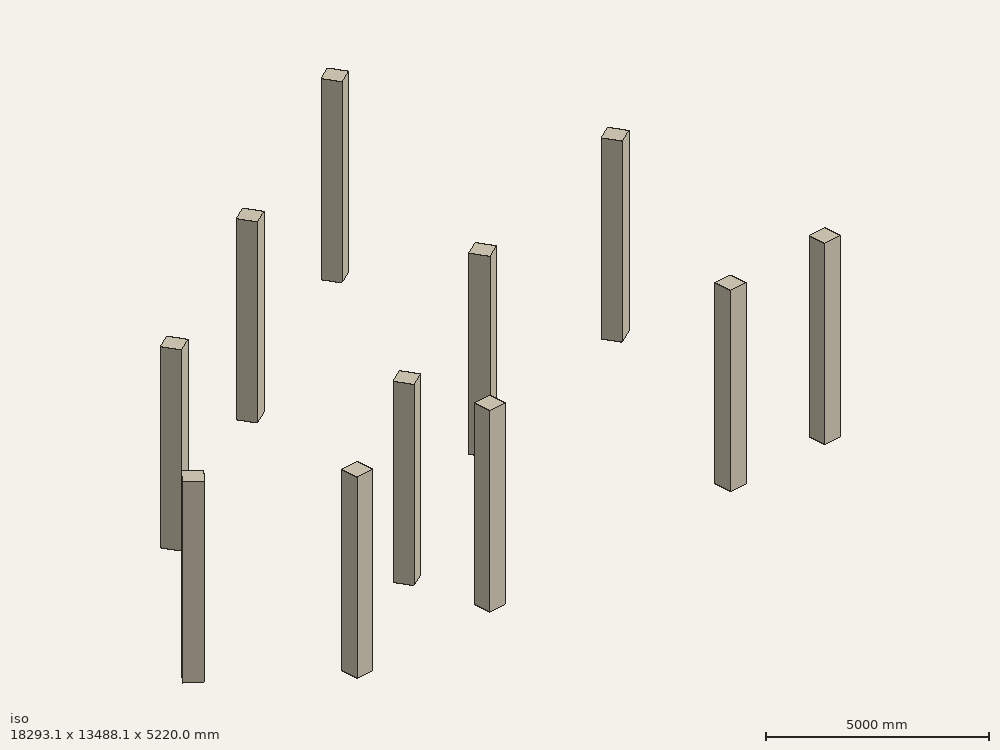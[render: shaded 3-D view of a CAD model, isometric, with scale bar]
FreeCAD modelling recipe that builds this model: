
FCSTD DOCUMENT  (FreeCAD 0.21R32165 (Git))
Label: test
License: All rights reserved
LicenseURL: http://en.wikipedia.org/wiki/All_rights_reserved
objects: Part::FeaturePython×27, Part::Part2DObjectPython×13, App::DocumentObjectGroup×2, App::FeaturePython×1
note: 40 computed .brp shape members not serialized (recipe doc carries the construction recipe); baked Part::Feature solids carry a one-line shape summary decoded from their .brp

FEATURE [Part::Part2DObjectPython] Line  label="C1_STORY1_CenterLine"  # Draft 2D object (typed FeaturePython)
  Area = 0
  ChamferSize = 0
  Closed = false
  End = (2820,0,5220)
  FilletRadius = 0
  Length = 5220
  MakeFace = true
  Points = (2) [(2820,0,0),(2820,0,5220)]
  Start = (2820,0,0)
  Subdivisions = 0
FEATURE [Part::Part2DObjectPython] C5016F20  # Draft 2D object (typed FeaturePython)
  Height = 500
  Width = 500
FEATURE [Part::FeaturePython] Structure  label="C1_STORY1"  # Arch/BIM 24 (typed FeaturePython)
  AttacherType = Attacher::AttachEngine3D
  AttachmentOffset = pos=(0,0,0) rot=(0,0,1;1.5708rad)
  Base = -> C5016F20
  BaseMirror = false
  BaseOffsetX = 0
  BaseOffsetY = 0
  BasePerpendicularToTool = false
  BaseRotation = 0
  ComputedLength = 5220
  FaceMaker = 0
  Height = 5220
  HorizontalArea = 250000
  IfcData = attributes={"GlobalId": {"name": "GlobalId", "type": "IfcGloballyUniqueId", "is_enum": false, "enum_values": []}, "Description": {"... (+438 chars omitted),+1 more (map truncated)
  IfcType = 24
  Length = 0
  MapMode = 7
  MoveBase = false
  MoveWithHost = false
  Nodes = (2) [(2820,0,0),(2820,0,5220)]
  NodesOffset = 0
  Normal = (0,0,0)
  PerimeterLength = 2000
  Placement = pos=(2820,0,0) rot=(0,0,1;1.5708rad)
  PredefinedType = 0
  Support = -> [Line]
  ToolOffsetFirst = 0
  ToolOffsetLast = 0
  VerticalArea = 1.044e+07
  Width = 100
  combos_load = COMB1 Max=367.7152, 16546.99, 15948.15,COMB10 Max=-248.3503, 396220.92, -73103.59,COMB11 Max=-87.283, 359070.73, 131552.42,+32 more (map truncated)
FEATURE [Part::Part2DObjectPython] Line001  label="C2_STORY1_CenterLine"  # Draft 2D object (typed FeaturePython)
  Area = 0
  ChamferSize = 0
  Closed = false
  End = (7040,0,5220)
  FilletRadius = 0
  Length = 5220
  MakeFace = true
  Points = (2) [(7040,0,0),(7040,0,5220)]
  Start = (7040,0,0)
  Subdivisions = 0
FEATURE [Part::FeaturePython] Structure001  label="C2_STORY1"  # Arch/BIM 24 (typed FeaturePython)
  AttacherType = Attacher::AttachEngine3D
  AttachmentOffset = pos=(0,0,0) rot=(0,0,1;1.5708rad)
  Base = -> C5016F20
  BaseMirror = false
  BaseOffsetX = 0
  BaseOffsetY = 0
  BasePerpendicularToTool = false
  BaseRotation = 0
  ComputedLength = 5220
  FaceMaker = 0
  Height = 5220
  HorizontalArea = 250000
  IfcData = attributes={"GlobalId": {"name": "GlobalId", "type": "IfcGloballyUniqueId", "is_enum": false, "enum_values": []}, "Description": {"... (+438 chars omitted),+1 more (map truncated)
  IfcType = 24
  Length = 0
  MapMode = 7
  MoveBase = false
  MoveWithHost = false
  Nodes = (2) [(7040,0,0),(7040,0,5220)]
  NodesOffset = 0
  Normal = (0,0,0)
  PerimeterLength = 2000
  Placement = pos=(7040,0,0) rot=(0,0,1;1.5708rad)
  PredefinedType = 0
  Support = -> [Line001]
  ToolOffsetFirst = 0
  ToolOffsetLast = 0
  VerticalArea = 1.044e+07
  Width = 100
  combos_load = COMB1 Max=587.8077, 16723.54, 23204.84,COMB10 Max=-181.5024, 376105.16, -60381.43,COMB11 Max=-325.9834, 365440.67, 122246.28,+32 more (map truncated)
FEATURE [Part::Part2DObjectPython] Line002  label="C3_STORY1_CenterLine"  # Draft 2D object (typed FeaturePython)
  Area = 0
  ChamferSize = 0
  Closed = false
  End = (14690,0,5220)
  FilletRadius = 0
  Length = 5220
  MakeFace = true
  Points = (2) [(14690,0,0),(14690,0,5220)]
  Start = (14690,0,0)
  Subdivisions = 0
FEATURE [Part::Part2DObjectPython] C5016F18  # Draft 2D object (typed FeaturePython)
  Height = 500
  Width = 500
FEATURE [Part::FeaturePython] Structure002  label="C3_STORY1"  # Arch/BIM 24 (typed FeaturePython)
  AttacherType = Attacher::AttachEngine3D
  AttachmentOffset = pos=(0,0,0) rot=(0,0,1;1.5708rad)
  Base = -> C5016F18
  BaseMirror = false
  BaseOffsetX = 0
  BaseOffsetY = 0
  BasePerpendicularToTool = false
  BaseRotation = 0
  ComputedLength = 5220
  FaceMaker = 0
  Height = 5220
  HorizontalArea = 250000
  IfcData = attributes={"GlobalId": {"name": "GlobalId", "type": "IfcGloballyUniqueId", "is_enum": false, "enum_values": []}, "Description": {"... (+438 chars omitted),+1 more (map truncated)
  IfcType = 24
  Length = 0
  MapMode = 7
  MoveBase = false
  MoveWithHost = false
  Nodes = (2) [(14690,0,0),(14690,0,5220)]
  NodesOffset = 0
  Normal = (0,0,0)
  PerimeterLength = 2000
  Placement = pos=(14690,0,0) rot=(0,0,1;1.5708rad)
  PredefinedType = 0
  Support = -> [Line002]
  ToolOffsetFirst = 0
  ToolOffsetLast = 0
  VerticalArea = 1.044e+07
  Width = 100
  combos_load = COMB1 Max=902.7233, -626.5, -12843.09,COMB10 Max=479.9441, 305538.87, -85269.26,COMB11 Max=651.8424, 341909.32, 114529.19,+32 more (map truncated)
FEATURE [Part::Part2DObjectPython] Line003  label="C4_STORY1_CenterLine"  # Draft 2D object (typed FeaturePython)
  Area = 0
  ChamferSize = 0
  Closed = false
  End = (17690,0,5220)
  FilletRadius = 0
  Length = 5220
  MakeFace = true
  Points = (2) [(17690,0,0),(17690,0,5220)]
  Start = (17690,0,0)
  Subdivisions = 0
FEATURE [Part::FeaturePython] Structure003  label="C4_STORY1"  # Arch/BIM 24 (typed FeaturePython)
  AttacherType = Attacher::AttachEngine3D
  AttachmentOffset = pos=(0,0,0) rot=(0,0,1;1.5708rad)
  Base = -> C5016F20
  BaseMirror = false
  BaseOffsetX = 0
  BaseOffsetY = 0
  BasePerpendicularToTool = false
  BaseRotation = 0
  ComputedLength = 5220
  FaceMaker = 0
  Height = 5220
  HorizontalArea = 250000
  IfcData = attributes={"GlobalId": {"name": "GlobalId", "type": "IfcGloballyUniqueId", "is_enum": false, "enum_values": []}, "Description": {"... (+438 chars omitted),+1 more (map truncated)
  IfcType = 24
  Length = 0
  MapMode = 7
  MoveBase = false
  MoveWithHost = false
  Nodes = (2) [(17690,0,0),(17690,0,5220)]
  NodesOffset = 0
  Normal = (0,0,0)
  PerimeterLength = 2000
  Placement = pos=(17690,0,0) rot=(0,0,1;1.5708rad)
  PredefinedType = 0
  Support = -> [Line003]
  ToolOffsetFirst = 0
  ToolOffsetLast = 0
  VerticalArea = 1.044e+07
  Width = 100
  combos_load = COMB1 Max=394.1757, -16386.34, 10448.1,COMB10 Max=369.9806, 284189.81, -78689.39,COMB11 Max=71.5353, 331138.48, 101835.87,+32 more (map truncated)
FEATURE [Part::Part2DObjectPython] Line004  label="C5_STORY1_CenterLine"  # Draft 2D object (typed FeaturePython)
  Area = 0
  ChamferSize = 0
  Closed = false
  End = (0,2400,5220)
  FilletRadius = 0
  Length = 5220
  MakeFace = true
  Points = (2) [(0,2400,0),(0,2400,5220)]
  Start = (0,2400,0)
  Subdivisions = 0
FEATURE [Part::FeaturePython] Structure004  label="C5_STORY1"  # Arch/BIM 24 (typed FeaturePython)
  AttacherType = Attacher::AttachEngine3D
  AttachmentOffset = pos=(0,0,0) rot=(0,0,1;2.40855rad)
  Base = -> C5016F20
  BaseMirror = false
  BaseOffsetX = 0
  BaseOffsetY = 0
  BasePerpendicularToTool = false
  BaseRotation = 0
  ComputedLength = 5220
  FaceMaker = 0
  Height = 5220
  HorizontalArea = 250000
  IfcData = attributes={"GlobalId": {"name": "GlobalId", "type": "IfcGloballyUniqueId", "is_enum": false, "enum_values": []}, "Description": {"... (+438 chars omitted),+1 more (map truncated)
  IfcType = 24
  Length = 0
  MapMode = 7
  MoveBase = false
  MoveWithHost = false
  Nodes = (2) [(0,2400,0),(0,2400,5220)]
  NodesOffset = 0
  Normal = (0,0,0)
  PerimeterLength = 2000
  Placement = pos=(0,2400,0) rot=(0,0,1;2.40855rad)
  PredefinedType = 0
  Support = -> [Line004]
  ToolOffsetFirst = 0
  ToolOffsetLast = 0
  VerticalArea = 1.044e+07
  Width = 100
  combos_load = COMB1 Max=845.9788, -2358.11, 12217.14,COMB10 Max=739.8057, 403960.89, -64360.33,COMB11 Max=978.3773, 349863.81, 118914.89,+32 more (map truncated)
FEATURE [Part::Part2DObjectPython] Line005  label="C6_STORY1_CenterLine"  # Draft 2D object (typed FeaturePython)
  Area = 0
  ChamferSize = 0
  Closed = false
  End = (6530,2130,5220)
  FilletRadius = 0
  Length = 5220
  MakeFace = true
  Points = (2) [(6530,2130,0),(6530,2130,5220)]
  Start = (6530,2130,0)
  Subdivisions = 0
FEATURE [Part::FeaturePython] Structure005  label="C6_STORY1"  # Arch/BIM 24 (typed FeaturePython)
  AttacherType = Attacher::AttachEngine3D
  AttachmentOffset = pos=(0,0,0) rot=(0,0,1;2.05949rad)
  Base = -> C5016F18
  BaseMirror = false
  BaseOffsetX = 0
  BaseOffsetY = 0
  BasePerpendicularToTool = false
  BaseRotation = 0
  ComputedLength = 5220
  FaceMaker = 0
  Height = 5220
  HorizontalArea = 250000
  IfcData = attributes={"GlobalId": {"name": "GlobalId", "type": "IfcGloballyUniqueId", "is_enum": false, "enum_values": []}, "Description": {"... (+438 chars omitted),+1 more (map truncated)
  IfcType = 24
  Length = 0
  MapMode = 7
  MoveBase = false
  MoveWithHost = false
  Nodes = (2) [(6530,2130,0),(6530,2130,5220)]
  NodesOffset = 0
  Normal = (0,0,0)
  PerimeterLength = 2000
  Placement = pos=(6530,2130,0) rot=(0,0,1;2.05949rad)
  PredefinedType = 0
  Support = -> [Line005]
  ToolOffsetFirst = 0
  ToolOffsetLast = 0
  VerticalArea = 10440000
  Width = 100
  combos_load = COMB1 Max=1142.9649, 7645.03, 13998.26,COMB10 Max=1675.2857, 442457.51, -98057.37,COMB11 Max=1614.6695, 416293.52, 104077.31,+32 more (map truncated)
FEATURE [Part::Part2DObjectPython] Line006  label="C7_STORY1_CenterLine"  # Draft 2D object (typed FeaturePython)
  Area = 0
  ChamferSize = 0
  Closed = false
  End = (11810,5000,5220)
  FilletRadius = 0
  Length = 5220
  MakeFace = true
  Points = (2) [(11810,5000,0),(11810,5000,5220)]
  Start = (11810,5000,0)
  Subdivisions = 0
FEATURE [Part::FeaturePython] Structure006  label="C7_STORY1"  # Arch/BIM 24 (typed FeaturePython)
  AttacherType = Attacher::AttachEngine3D
  AttachmentOffset = pos=(0,0,0) rot=(0,0,1;2.05949rad)
  Base = -> C5016F18
  BaseMirror = false
  BaseOffsetX = 0
  BaseOffsetY = 0
  BasePerpendicularToTool = false
  BaseRotation = 0
  ComputedLength = 5220
  FaceMaker = 0
  Height = 5220
  HorizontalArea = 250000
  IfcData = attributes={"GlobalId": {"name": "GlobalId", "type": "IfcGloballyUniqueId", "is_enum": false, "enum_values": []}, "Description": {"... (+438 chars omitted),+1 more (map truncated)
  IfcType = 24
  Length = 0
  MapMode = 7
  MoveBase = false
  MoveWithHost = false
  Nodes = (2) [(11810,5000,0),(11810,5000,5220)]
  NodesOffset = 0
  Normal = (0,0,0)
  PerimeterLength = 2000
  Placement = pos=(11810,5000,0) rot=(0,0,1;2.05949rad)
  PredefinedType = 0
  Support = -> [Line006]
  ToolOffsetFirst = 0
  ToolOffsetLast = 0
  VerticalArea = 10440000
  Width = 100
  combos_load = COMB1 Max=1470.3846, 25607.06, -7248.47,COMB10 Max=1241.0286, 398976.99, -113320.28,COMB11 Max=1252.6058, 418711.74, 111040.08,+32 more (map truncated)
FEATURE [Part::Part2DObjectPython] Line007  label="C15_STORY1_CenterLine"  # Draft 2D object (typed FeaturePython)
  Area = 0
  ChamferSize = 0
  Closed = false
  End = (17580,6560,5220)
  FilletRadius = 0
  Length = 5220
  MakeFace = true
  Points = (2) [(17580,6560,0),(17580,6560,5220)]
  Start = (17580,6560,0)
  Subdivisions = 0
FEATURE [Part::FeaturePython] Structure007  label="C15_STORY1"  # Arch/BIM 24 (typed FeaturePython)
  AttacherType = Attacher::AttachEngine3D
  AttachmentOffset = pos=(0,0,0) rot=(0,0,1;2.05949rad)
  Base = -> C5016F20
  BaseMirror = false
  BaseOffsetX = 0
  BaseOffsetY = 0
  BasePerpendicularToTool = false
  BaseRotation = 0
  ComputedLength = 5220
  FaceMaker = 0
  Height = 5220
  HorizontalArea = 250000
  IfcData = attributes={"GlobalId": {"name": "GlobalId", "type": "IfcGloballyUniqueId", "is_enum": false, "enum_values": []}, "Description": {"... (+438 chars omitted),+1 more (map truncated)
  IfcType = 24
  Length = 0
  MapMode = 7
  MoveBase = false
  MoveWithHost = false
  Nodes = (2) [(17580,6560,0),(17580,6560,5220)]
  NodesOffset = 0
  Normal = (0,0,0)
  PerimeterLength = 2000
  Placement = pos=(17580,6560,0) rot=(0,0,1;2.05949rad)
  PredefinedType = 0
  Support = -> [Line007]
  ToolOffsetFirst = 0
  ToolOffsetLast = 0
  VerticalArea = 10440000
  Width = 100
  combos_load = COMB1 Max=1023.3813, -5129.39, -10588.01,COMB10 Max=996.5272, 331820.48, -118135.48,COMB11 Max=868.507, 387152.71, 87509.08,+32 more (map truncated)
FEATURE [Part::Part2DObjectPython] Line008  label="C12_STORY1_CenterLine"  # Draft 2D object (typed FeaturePython)
  Area = 0
  ChamferSize = 0
  Closed = false
  End = (3930,6930,5220)
  FilletRadius = 0
  Length = 5220
  MakeFace = true
  Points = (2) [(3930,6930,0),(3930,6930,5220)]
  Start = (3930,6930,0)
  Subdivisions = 0
FEATURE [Part::FeaturePython] Structure008  label="C12_STORY1"  # Arch/BIM 24 (typed FeaturePython)
  AttacherType = Attacher::AttachEngine3D
  AttachmentOffset = pos=(0,0,0) rot=(0,0,1;2.05949rad)
  Base = -> C5016F18
  BaseMirror = false
  BaseOffsetX = 0
  BaseOffsetY = 0
  BasePerpendicularToTool = false
  BaseRotation = 0
  ComputedLength = 5220
  FaceMaker = 0
  Height = 5220
  HorizontalArea = 250000
  IfcData = attributes={"GlobalId": {"name": "GlobalId", "type": "IfcGloballyUniqueId", "is_enum": false, "enum_values": []}, "Description": {"... (+438 chars omitted),+1 more (map truncated)
  IfcType = 24
  Length = 0
  MapMode = 7
  MoveBase = false
  MoveWithHost = false
  Nodes = (2) [(3930,6930,0),(3930,6930,5220)]
  NodesOffset = 0
  Normal = (0,0,0)
  PerimeterLength = 2000
  Placement = pos=(3930,6930,0) rot=(0,0,1;2.05949rad)
  PredefinedType = 0
  Support = -> [Line008]
  ToolOffsetFirst = 0
  ToolOffsetLast = 0
  VerticalArea = 10440000
  Width = 100
  combos_load = COMB1 Max=1247.9579, 23164.82, -18517.45,COMB10 Max=1381.272, 424798.86, -153063.06,COMB11 Max=1393.9715, 378913.68, 61467.35,+32 more (map truncated)
FEATURE [Part::Part2DObjectPython] Line009  label="C13_STORY1_CenterLine"  # Draft 2D object (typed FeaturePython)
  Area = 0
  ChamferSize = 0
  Closed = false
  End = (9210,9790,5220)
  FilletRadius = 0
  Length = 5220
  MakeFace = true
  Points = (2) [(9210,9790,0),(9210,9790,5220)]
  Start = (9210,9790,0)
  Subdivisions = 0
FEATURE [Part::FeaturePython] Structure009  label="C13_STORY1"  # Arch/BIM 24 (typed FeaturePython)
  AttacherType = Attacher::AttachEngine3D
  AttachmentOffset = pos=(0,0,0) rot=(0,0,1;2.05949rad)
  Base = -> C5016F18
  BaseMirror = false
  BaseOffsetX = 0
  BaseOffsetY = 0
  BasePerpendicularToTool = false
  BaseRotation = 0
  ComputedLength = 5220
  FaceMaker = 0
  Height = 5220
  HorizontalArea = 250000
  IfcData = attributes={"GlobalId": {"name": "GlobalId", "type": "IfcGloballyUniqueId", "is_enum": false, "enum_values": []}, "Description": {"... (+438 chars omitted),+1 more (map truncated)
  IfcType = 24
  Length = 0
  MapMode = 7
  MoveBase = false
  MoveWithHost = false
  Nodes = (2) [(9210,9790,0),(9210,9790,5220)]
  NodesOffset = 0
  Normal = (0,0,0)
  PerimeterLength = 2000
  Placement = pos=(9210,9790,0) rot=(0,0,1;2.05949rad)
  PredefinedType = 0
  Support = -> [Line009]
  ToolOffsetFirst = 0
  ToolOffsetLast = 0
  VerticalArea = 10440000
  Width = 100
  combos_load = COMB1 Max=1220.7803, 12910.2, -5796.66,COMB10 Max=1204.0061, 368069.87, -155855.13,COMB11 Max=1270.787, 356109, 83573.62,+32 more (map truncated)
FEATURE [Part::Part2DObjectPython] Line010  label="C14_STORY1_CenterLine"  # Draft 2D object (typed FeaturePython)
  Area = 0
  ChamferSize = 0
  Closed = false
  End = (15010,12900,5220)
  FilletRadius = 0
  Length = 5220
  MakeFace = true
  Points = (2) [(15010,12900,0),(15010,12900,5220)]
  Start = (15010,12900,0)
  Subdivisions = 0
FEATURE [Part::FeaturePython] Structure010  label="C14_STORY1"  # Arch/BIM 24 (typed FeaturePython)
  AttacherType = Attacher::AttachEngine3D
  AttachmentOffset = pos=(0,0,0) rot=(0,0,1;2.05949rad)
  Base = -> C5016F20
  BaseMirror = false
  BaseOffsetX = 0
  BaseOffsetY = 0
  BasePerpendicularToTool = false
  BaseRotation = 0
  ComputedLength = 5220
  FaceMaker = 0
  Height = 5220
  HorizontalArea = 250000
  IfcData = attributes={"GlobalId": {"name": "GlobalId", "type": "IfcGloballyUniqueId", "is_enum": false, "enum_values": []}, "Description": {"... (+438 chars omitted),+1 more (map truncated)
  IfcType = 24
  Length = 0
  MapMode = 7
  MoveBase = false
  MoveWithHost = false
  Nodes = (2) [(15010,12900,0),(15010,12900,5220)]
  NodesOffset = 0
  Normal = (0,0,0)
  PerimeterLength = 2000
  Placement = pos=(15010,12900,0) rot=(0,0,1;2.05949rad)
  PredefinedType = 0
  Support = -> [Line010]
  ToolOffsetFirst = 0
  ToolOffsetLast = 0
  VerticalArea = 10440000
  Width = 100
  combos_load = COMB1 Max=1046.0824, 31702.53, 18752.72,COMB10 Max=1146.1247, 337869.44, -132552.97,COMB11 Max=1115.0926, 366884.94, 102704.55,+32 more (map truncated)
FEATURE [App::DocumentObjectGroup] Columns
  Group = -> [Structure,Structure001,Structure002,Structure003,Structure004,Structure005,Structure006,Structure007,Structure008,Structure009,Structure010]
FEATURE [Part::FeaturePython] Beam  # WARN: FeaturePython — macro-defined, semantics opaque (R4)
  end_point = (7040,0,0)
  start_point = (2820,0,0)
FEATURE [Part::FeaturePython] Beam001  # WARN: FeaturePython — macro-defined, semantics opaque (R4)
  end_point = (14690,0,0)
  start_point = (7040,0,0)
FEATURE [Part::FeaturePython] Beam002  # WARN: FeaturePython — macro-defined, semantics opaque (R4)
  end_point = (17690,0,0)
  start_point = (14690,0,0)
FEATURE [Part::FeaturePython] Beam003  # WARN: FeaturePython — macro-defined, semantics opaque (R4)
  end_point = (6530,2130,0)
  start_point = (2820,0,0)
FEATURE [Part::FeaturePython] Beam004  # WARN: FeaturePython — macro-defined, semantics opaque (R4)
  end_point = (11810,5000,0)
  start_point = (6530,2130,0)
FEATURE [Part::FeaturePython] Beam005  # WARN: FeaturePython — macro-defined, semantics opaque (R4)
  end_point = (17580,6560,0)
  start_point = (11810,5000,0)
FEATURE [Part::FeaturePython] Beam006  # WARN: FeaturePython — macro-defined, semantics opaque (R4)
  end_point = (7040,0,0)
  start_point = (6530,2130,0)
FEATURE [Part::FeaturePython] Beam007  # WARN: FeaturePython — macro-defined, semantics opaque (R4)
  end_point = (6530,2130,0)
  start_point = (3930,6930,0)
FEATURE [Part::FeaturePython] Beam008  # WARN: FeaturePython — macro-defined, semantics opaque (R4)
  end_point = (14690,0,0)
  start_point = (11810,5000,0)
FEATURE [Part::FeaturePython] Beam009  # WARN: FeaturePython — macro-defined, semantics opaque (R4)
  end_point = (11810,5000,0)
  start_point = (9210,9790,0)
FEATURE [Part::FeaturePython] Beam010  # WARN: FeaturePython — macro-defined, semantics opaque (R4)
  end_point = (17580,6560,0)
  start_point = (17690,0,0)
FEATURE [Part::FeaturePython] Beam011  # WARN: FeaturePython — macro-defined, semantics opaque (R4)
  end_point = (17580,6560,0)
  start_point = (15010,12900,0)
FEATURE [Part::FeaturePython] Beam012  # WARN: FeaturePython — macro-defined, semantics opaque (R4)
  end_point = (3930,6930,0)
  start_point = (0,2400,0)
FEATURE [Part::FeaturePython] Beam013  # WARN: FeaturePython — macro-defined, semantics opaque (R4)
  end_point = (9210,9790,0)
  start_point = (3930,6930,0)
FEATURE [Part::FeaturePython] Beam014  # WARN: FeaturePython — macro-defined, semantics opaque (R4)
  end_point = (15010,12900,0)
  start_point = (9210,9790,0)
FEATURE [Part::FeaturePython] Beam016  # WARN: FeaturePython — macro-defined, semantics opaque (R4)
  end_point = (2820,0,0)
  start_point = (0,2400,0)
FEATURE [App::DocumentObjectGroup] Beams
  Group = -> [Beam,Beam001,Beam002,Beam003,Beam004,Beam005,Beam006,Beam007,Beam008,Beam009,Beam010,Beam011,Beam012,Beam013,Beam014,Beam016]
FEATURE [App::FeaturePython] Safe  # WARN: FeaturePython — macro-defined, semantics opaque (R4)
  input = <path>
  output = <path>
note: 2 file-system paths scrubbed to <path> (originals preserved in the JSON sidecar)
